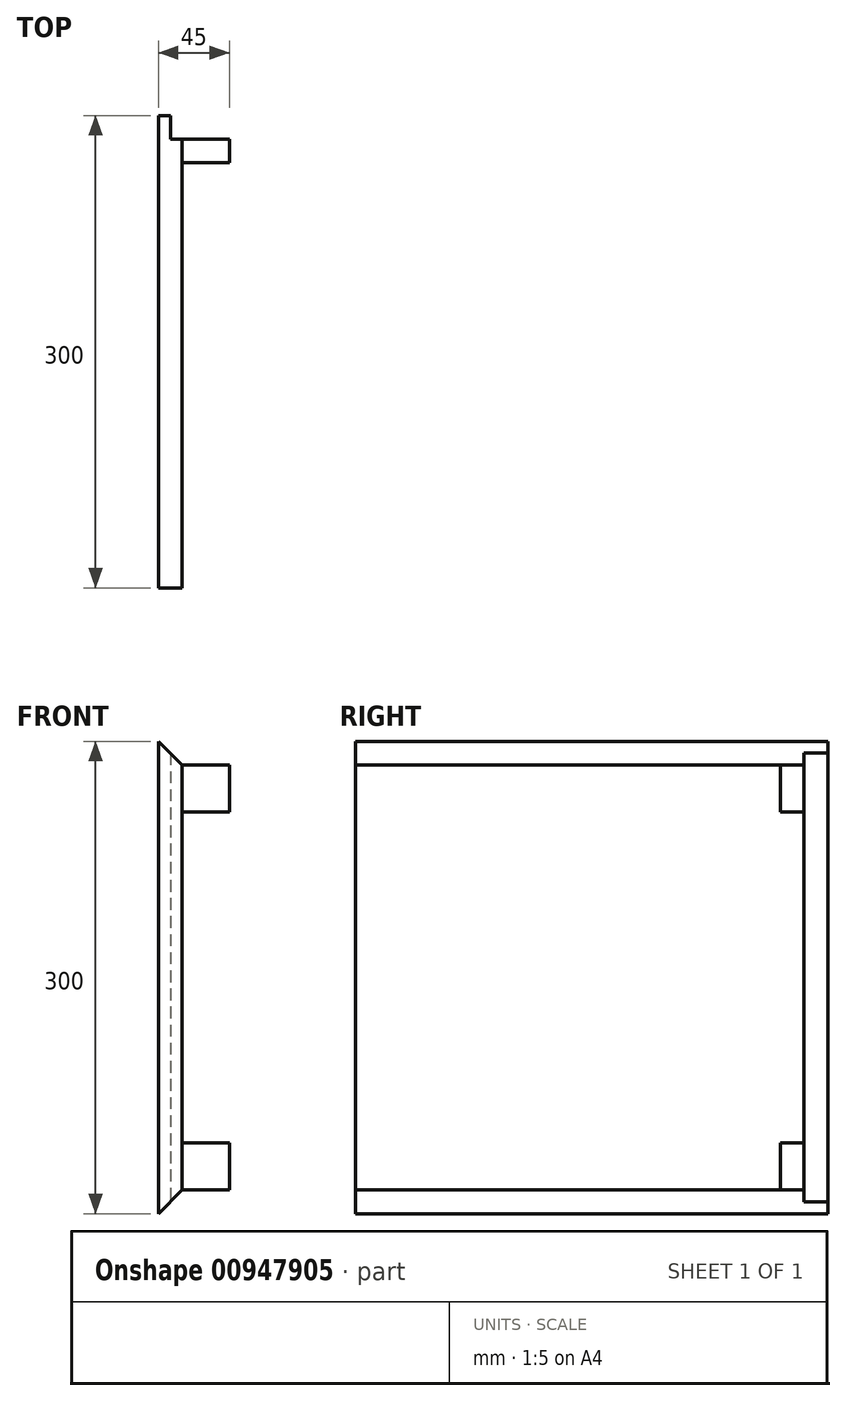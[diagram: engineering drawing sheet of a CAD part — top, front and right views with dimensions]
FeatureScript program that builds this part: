
annotation { "Feature Type Name" : "Feature", "Feature Type Description" : "" }
export const myFeature = defineFeature(function(context is Context, id is Id, definition is map)
    precondition{}
    {
        {
            var Q0;
            Q0=qCreatedBy(makeId("Right.planeOp"),FACE);
            cPlane(context, id + "F0", {"entities" : qUnion([Q0]), "cplaneType" : CPlaneType.OFFSET, "offset" : 100 * mm, "oppositeDirection" : true, "width" : 150 * mm, "height" : 150 * mm});
        }
        {
            var Q0;
            Q0=qCreatedBy(makeId("Top.planeOp"),FACE);
            cPlane(context, id + "F1", {"entities" : qUnion([Q0]), "cplaneType" : CPlaneType.OFFSET, "offset" : 300 * mm, "width" : 150 * mm, "height" : 150 * mm});
        }
        {
            var Q0;
            Q0=qCreatedBy(makeId("Front.planeOp"),FACE);
            var sketch = newSketch(context, id + "F2", { "sketchPlane" : qUnion([Q0])});
            skLineSegment(sketch, "E0", {"start": v(-100, 0) * mm, "end": v(-100, 300) * mm});
            skLineSegment(sketch, "E1", {"start": v(-100, 300) * mm, "end": v(-85, 285) * mm});
            skLineSegment(sketch, "E2", {"start": v(-85, 285) * mm, "end": v(-85, 15) * mm});
            skLineSegment(sketch, "E3", {"start": v(-85, 15) * mm, "end": v(-100, 0) * mm});
            skSolve(sketch);
        }
        {
            var Q0;
            Q0=qCreatedBy(makeId("Front.planeOp"),FACE);
            cPlane(context, id + "F3", {"entities" : qUnion([Q0]), "cplaneType" : CPlaneType.OFFSET, "offset" : 150 * mm, "width" : 150 * mm, "height" : 150 * mm});
        }
        {
            var Q0;
            Q0=qCreatedBy(makeId("Front.planeOp"),FACE);
            cPlane(context, id + "F4", {"entities" : qUnion([Q0]), "cplaneType" : CPlaneType.OFFSET, "offset" : 150 * mm, "oppositeDirection" : true, "width" : 150 * mm, "height" : 150 * mm});
        }
        {
            var Q0;
            Q0=makeQuery(id+"F2.imprint","IMPRINT",FACE,{"disambiguationData":[TD([[makeQuery(id+"F2.imprint","IMPRINT",EDGE,{"derivedFrom":sQuery(id+"F2.wireOp",EDGE,"E0")}),-1.0]])]});
            var Q1;
            Q1=qCreatedBy(id+"F4.planeOp",FACE);
            var Q2;
            Q2=qCreatedBy(id+"F3.planeOp",FACE);
            extrude(context, id + "F5", {"entities" : qUnion([Q0]), "endBound" : BoundingType.UP_TO_SURFACE, "oppositeDirection" : true, "depth" : 25 * mm, "endBoundEntityFace" : qUnion([Q1]), "offsetDistance" : 25 * mm, "hasSecondDirection" : true, "secondDirectionBound" : BoundingType.UP_TO_SURFACE, "secondDirectionOppositeDirection" : false, "secondDirectionDepth" : 25 * mm, "secondDirectionBoundEntityFace" : qUnion([Q2])});
        }
        {
            var Q0;
            Q0=qCreatedBy(id+"F4.planeOp",FACE);
            var sketch = newSketch(context, id + "F6", { "sketchPlane" : qUnion([Q0])});
            skLineSegment(sketch, "E4.bottom", {"start": v(-80, 300) * mm, "end": v(-92.5, 300) * mm});
            skLineSegment(sketch, "E4.top", {"start": v(-80, 0) * mm, "end": v(-92.5, 0) * mm});
            skLineSegment(sketch, "E4.left", {"start": v(-80, 300) * mm, "end": v(-80, 0) * mm});
            skLineSegment(sketch, "E4.right", {"start": v(-92.5, 300) * mm, "end": v(-92.5, 0) * mm});
            skSolve(sketch);
        }
        {
            var Q0;
            Q0 = qSketchRegion(id + "F6", true);
            extrude(context, id + "F7", {"entities" : qUnion([Q0]), "operationType" : NewBodyOperationType.REMOVE, "depth" : 15 * mm, "offsetDistance" : 25 * mm});
        }
        {
            var Q0;
            Q0=qCreatedBy(makeId("Front.planeOp"),FACE);
            cPlane(context, id + "F8", {"entities" : qUnion([Q0]), "cplaneType" : CPlaneType.OFFSET, "offset" : (150 - 15) * mm, "oppositeDirection" : true, "width" : 150 * mm, "height" : 150 * mm});
        }
        {
            var Q0;
            Q0=qCreatedBy(id+"F8.planeOp",FACE);
            var sketch = newSketch(context, id + "F9", { "sketchPlane" : qUnion([Q0])});
            skLineSegment(sketch, "E5.bottom", {"start": v(-85, 285) * mm, "end": v(-55, 285) * mm});
            skLineSegment(sketch, "E5.top", {"start": v(-85, 255) * mm, "end": v(-55, 255) * mm});
            skLineSegment(sketch, "E5.left", {"start": v(-85, 285) * mm, "end": v(-85, 255) * mm});
            skLineSegment(sketch, "E5.right", {"start": v(-55, 285) * mm, "end": v(-55, 255) * mm});
            skLineSegment(sketch, "E6.bottom", {"start": v(-85, 15) * mm, "end": v(-55, 15) * mm});
            skLineSegment(sketch, "E6.top", {"start": v(-85, 45) * mm, "end": v(-55, 45) * mm});
            skLineSegment(sketch, "E6.left", {"start": v(-85, 15) * mm, "end": v(-85, 45) * mm});
            skLineSegment(sketch, "E6.right", {"start": v(-55, 15) * mm, "end": v(-55, 45) * mm});
            skSolve(sketch);
        }
        {
            var Q0;
            Q0 = qSketchRegion(id + "F9", true);
            extrude(context, id + "F10", {"entities" : qUnion([Q0]), "operationType" : NewBodyOperationType.ADD, "depth" : 15 * mm, "offsetDistance" : 25 * mm});
        }
    });
